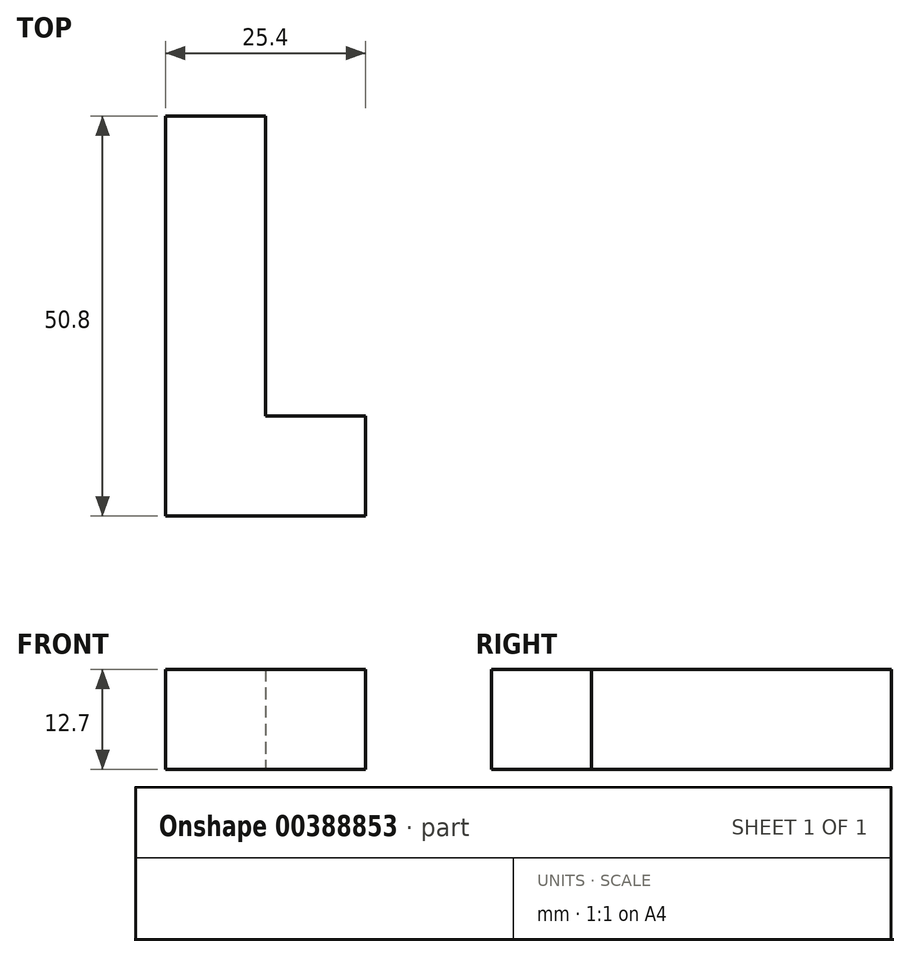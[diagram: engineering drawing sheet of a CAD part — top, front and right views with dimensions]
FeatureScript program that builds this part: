
annotation { "Feature Type Name" : "Feature", "Feature Type Description" : "" }
export const myFeature = defineFeature(function(context is Context, id is Id, definition is map)
    precondition{}
    {
        {
            var Q0;
            Q0=qCreatedBy(makeId("Top.planeOp"),FACE);
            var sketch = newSketch(context, id + "F0", { "sketchPlane" : qUnion([Q0])});
            skLineSegment(sketch, "E0.bottom", {"start": v(0, 0) * mm, "end": v(-12.7, 0) * mm});
            skLineSegment(sketch, "E0.top", {"start": v(0, 50.8) * mm, "end": v(-12.7, 50.8) * mm});
            skLineSegment(sketch, "E0.left", {"start": v(0, 12.7) * mm, "end": v(0, 50.8) * mm});
            skLineSegment(sketch, "E0.right", {"start": v(-12.7, 0) * mm, "end": v(-12.7, 50.8) * mm});
            skLineSegment(sketch, "E1.bottom", {"start": v(0, 0) * mm, "end": v(12.7, 0) * mm});
            skLineSegment(sketch, "E1.top", {"start": v(0, 12.7) * mm, "end": v(12.7, 12.7) * mm});
            skLineSegment(sketch, "E1.right", {"start": v(12.7, 0) * mm, "end": v(12.7, 12.7) * mm});
            skSolve(sketch);
        }
        {
            var Q0;
            Q0=makeQuery(id+"F0.imprint","IMPRINT",FACE,{"disambiguationData":[TD([[makeQuery(id+"F0.imprint","IMPRINT",EDGE,{"derivedFrom":sQuery(id+"F0.wireOp",EDGE,"E0.bottom")}),-1.0]])]});
            extrude(context, id + "F1", {"entities" : qUnion([Q0]), "depth" : 12.7 * mm});
        }
    });
